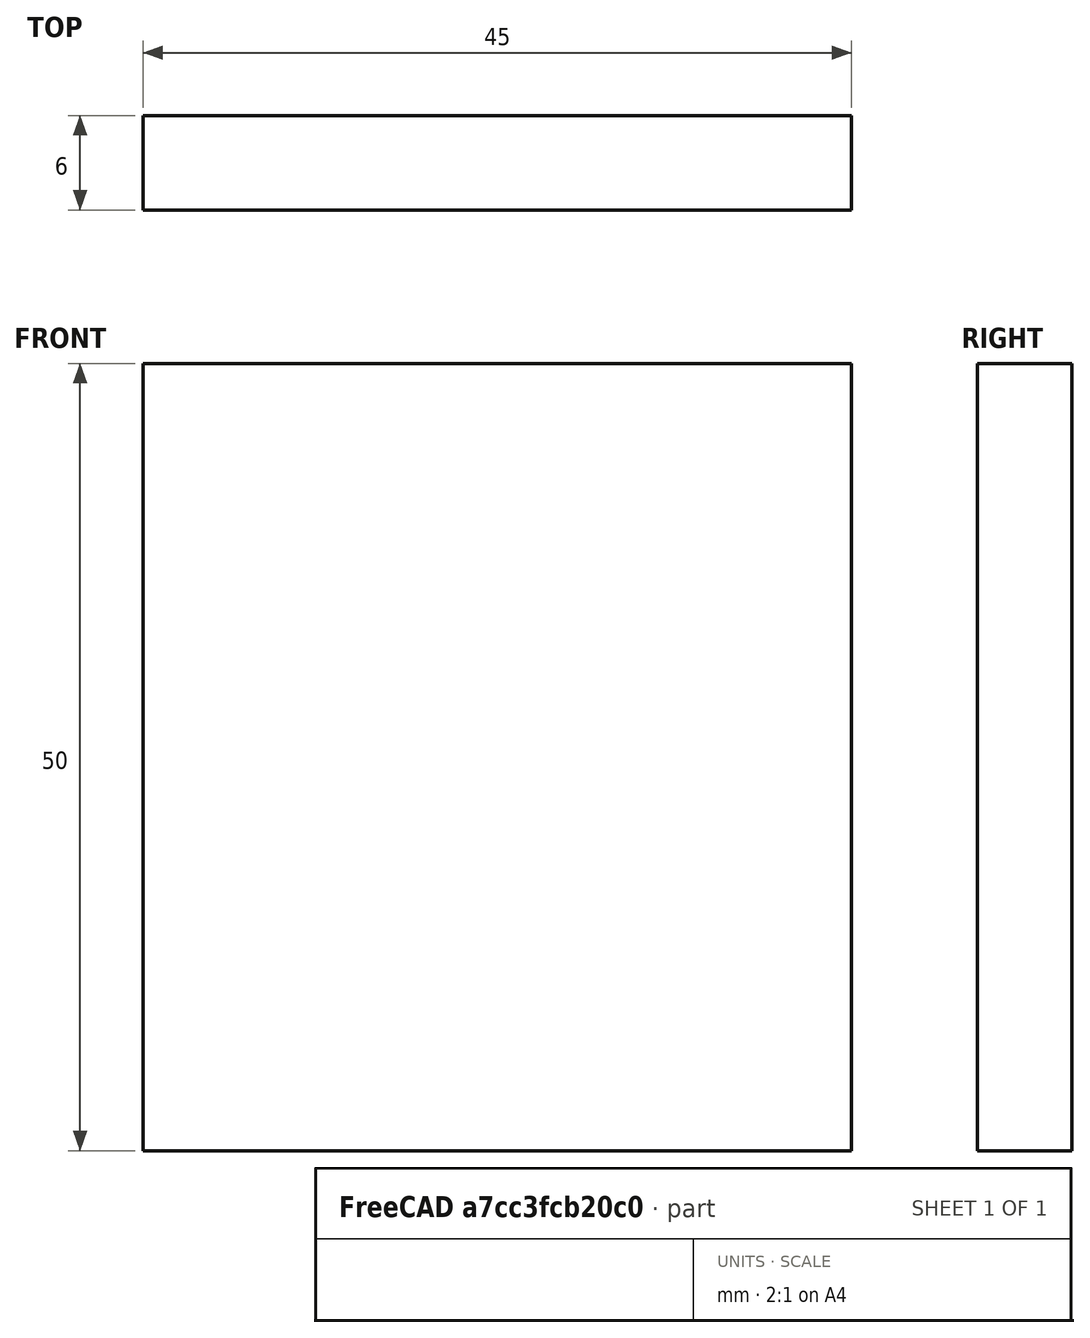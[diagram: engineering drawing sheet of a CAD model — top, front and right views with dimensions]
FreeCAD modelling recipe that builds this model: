
FCSTD DOCUMENT  (FreeCAD 0.15R4671 (Git))
Label: Flat Bar 45x6 EN10058 S235JR
License: All rights reserved
LicenseURL: http://en.wikipedia.org/wiki/All_rights_reserved
objects: Sketcher::SketchObject×1, Part::Extrusion×1
note: 2 computed .brp shape members not serialized (recipe doc carries the construction recipe); baked Part::Feature solids carry a one-line shape summary decoded from their .brp

FEATURE [Sketcher::SketchObject] Sketch
  sketch-geometry (4):
    g0: LineSegment StartX=-22.5 StartY=-3 StartZ=0 EndX=22.5 EndY=-3 EndZ=0
    g1: LineSegment StartX=22.5 StartY=-3 StartZ=0 EndX=22.5 EndY=3 EndZ=0
    g2: LineSegment StartX=22.5 StartY=3 StartZ=0 EndX=-22.5 EndY=3 EndZ=0
    g3: LineSegment StartX=-22.5 StartY=3 StartZ=0 EndX=-22.5 EndY=-3 EndZ=0
  constraints (12):
    c: Coincident(g0,g1)
    c: Coincident(g1,g2)
    c: Coincident(g2,g3)
    c: Coincident(g3,g0)
    c: Horizontal(g0)
    c: Horizontal(g2)
    c: Vertical(g1)
    c: Vertical(g3)
    c: Symmetric(g1,g2,g-2)
    c: Symmetric(g0,g1,g-1)
    c: DistanceY(g1) = 6
    c: DistanceX(g0) = 45
FEATURE [Part::Extrusion] Extrude  label="Flat Bar 45x6 EN10058 S235JR"
  Base = -> Sketch
  Dir = (0,0,50)
  Solid = true
